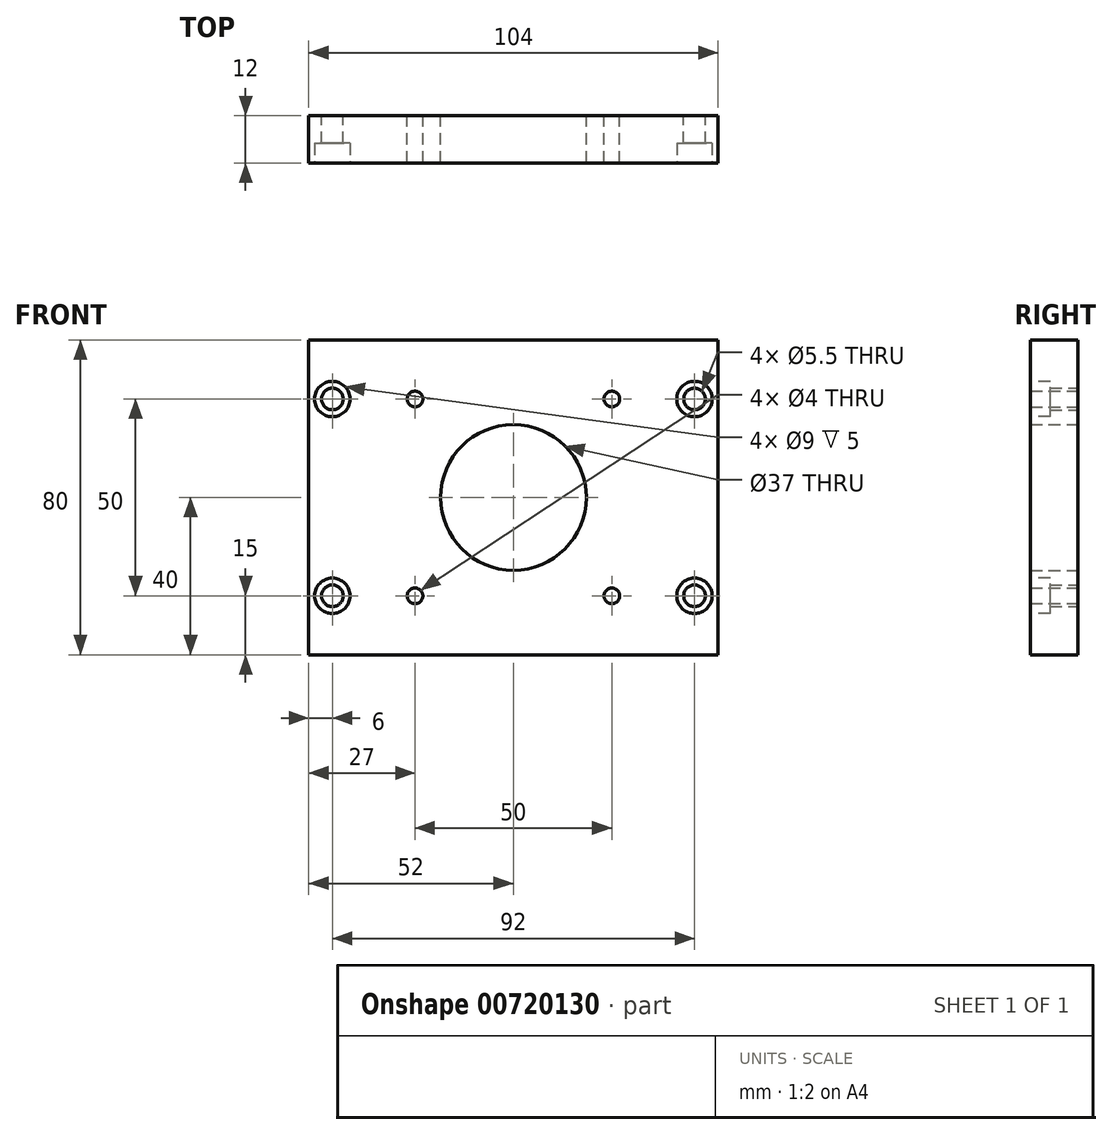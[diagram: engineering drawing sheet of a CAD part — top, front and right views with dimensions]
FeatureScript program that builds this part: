
annotation { "Feature Type Name" : "Feature", "Feature Type Description" : "" }
export const myFeature = defineFeature(function(context is Context, id is Id, definition is map)
    precondition{}
    {
        {
            var Q0;
            Q0=qCreatedBy(makeId("Front.planeOp"),FACE);
            var sketch = newSketch(context, id + "F0", { "sketchPlane" : qUnion([Q0])});
            skLineSegment(sketch, "E0.bottom", {"start": v(0, 0) * mm, "end": v(104, 0) * mm});
            skLineSegment(sketch, "E0.top", {"start": v(0, 80) * mm, "end": v(104, 80) * mm});
            skLineSegment(sketch, "E0.left", {"start": v(0, 0) * mm, "end": v(0, 80) * mm});
            skLineSegment(sketch, "E0.right", {"start": v(104, 0) * mm, "end": v(104, 80) * mm});
            skCircle(sketch, "E1", {"center": v(52, 40) * mm, "radius": 18.5 * mm});
            skPoint(sketch, "E1.centerSnap0", {"position": v(104, 40) * mm});
            skPoint(sketch, "E1.centerSnap1", {"position": v(52, 80) * mm});
            skCircle(sketch, "E2", {"center": v(6, 15) * mm, "radius": 2.75 * mm});
            skCircle(sketch, "E3", {"center": v(6, 65) * mm, "radius": 2.75 * mm});
            skCircle(sketch, "E4", {"center": v(98, 65) * mm, "radius": 2.75 * mm});
            skCircle(sketch, "E5", {"center": v(98, 15) * mm, "radius": 2.75 * mm});
            skCircle(sketch, "E6", {"center": v(27, 65) * mm, "radius": 2 * mm});
            skCircle(sketch, "E7.0.1.0", {"center": v(27, 15) * mm, "radius": 2 * mm});
            skCircle(sketch, "E7.1.0.0", {"center": v(77, 65) * mm, "radius": 2 * mm});
            skCircle(sketch, "E7.1.1.0", {"center": v(77, 15) * mm, "radius": 2 * mm});
            skLineSegment(sketch, "E7.direction1", {"start": v(27, 65) * mm, "end": v(77, 65) * mm, "construction": true});
            skLineSegment(sketch, "E7.direction2", {"start": v(27, 65) * mm, "end": v(27, 15) * mm, "construction": true});
            skSolve(sketch);
        }
        {
            var Q0;
            Q0=makeQuery(id+"F0.imprint","IMPRINT",FACE,{"disambiguationData":[TD([[makeQuery(id+"F0.imprint","IMPRINT",EDGE,{"derivedFrom":sQuery(id+"F0.wireOp",EDGE,"E0.bottom")}),1.0]])]});
            extrude(context, id + "F1", {"entities" : qUnion([Q0]), "depth" : 12 * mm, "offsetDistance" : 25 * mm});
        }
        {
            var Q0;
            Q0=makeQuery(id+"F1.opExtrude","CAP_FACE",FACE,{"disambiguationData":[OSD([sQuery(id+"F0.wireOp",EDGE,"E0.bottom"),sQuery(id+"F0.wireOp",EDGE,"E0.top"),sQuery(id+"F0.wireOp",EDGE,"E0.left"),sQuery(id+"F0.wireOp",EDGE,"E0.right"),sQuery(id+"F0.wireOp",EDGE,"E1"),sQuery(id+"F0.wireOp",EDGE,"E2"),sQuery(id+"F0.wireOp",EDGE,"E3"),sQuery(id+"F0.wireOp",EDGE,"E4"),sQuery(id+"F0.wireOp",EDGE,"E5")])],"isStart":false});
            var sketch = newSketch(context, id + "F2", { "sketchPlane" : qUnion([Q0])});
            skCircle(sketch, "E8", {"center": v(6, 65) * mm, "radius": 4.5 * mm});
            skCircle(sketch, "E9", {"center": v(98, 65) * mm, "radius": 4.5 * mm});
            skCircle(sketch, "E10", {"center": v(98, 15) * mm, "radius": 4.5 * mm});
            skCircle(sketch, "E11", {"center": v(6, 15) * mm, "radius": 4.5 * mm});
            skSolve(sketch);
        }
        {
            var Q0;
            Q0 = qSketchRegion(id + "F2", true);
            extrude(context, id + "F3", {"entities" : qUnion([Q0]), "operationType" : NewBodyOperationType.REMOVE, "oppositeDirection" : true, "depth" : 5 * mm, "offsetDistance" : 25 * mm});
        }
    });
